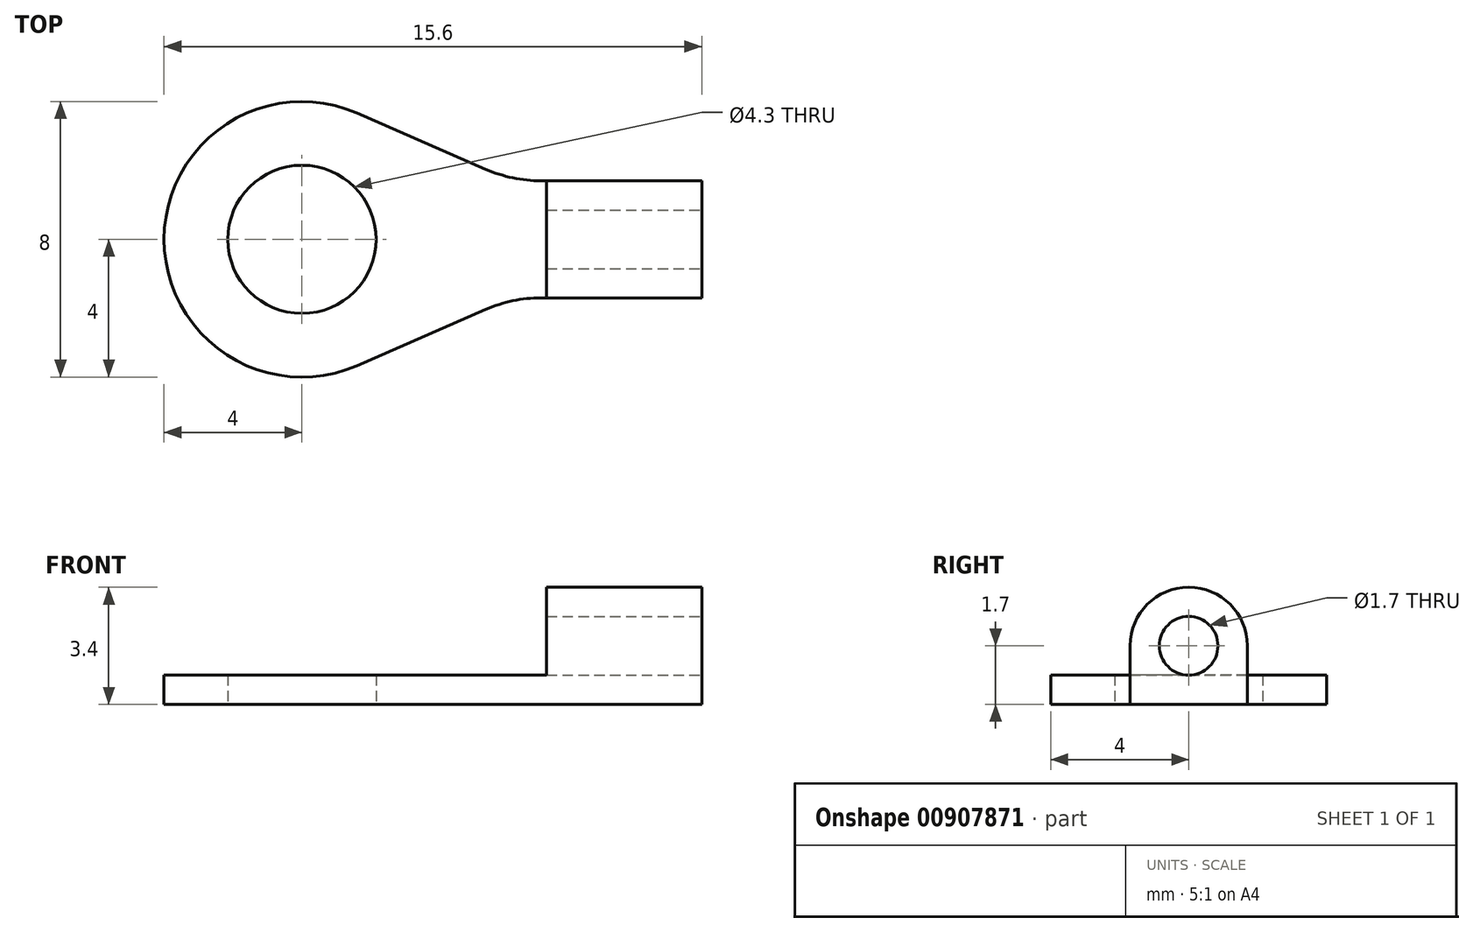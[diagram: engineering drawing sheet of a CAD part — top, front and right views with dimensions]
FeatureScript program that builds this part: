
annotation { "Feature Type Name" : "Feature", "Feature Type Description" : "" }
export const myFeature = defineFeature(function(context is Context, id is Id, definition is map)
    precondition{}
    {
        {
            var Q0;
            Q0=qCreatedBy(makeId("Top.planeOp"),FACE);
            var sketch = newSketch(context, id + "F0", { "sketchPlane" : qUnion([Q0])});
            skLineSegment(sketch, "E0.left", {"start": v(0, 4) * mm, "end": v(0, 4) * mm});
            skLineSegment(sketch, "E0.right", {"start": v(15.6, 2.3) * mm, "end": v(15.6, 5.7) * mm});
            skPoint(sketch, "E1.visualSharp", {"position": v(0, 8) * mm});
            skArc(sketch, "E1.filletArc", {"start": v(4, 8) * mm, "mid": v(1.17, 6.83) * mm, "end": v(0, 4) * mm});
            skPoint(sketch, "E2.visualSharp", {"position": v(0, 0) * mm});
            skArc(sketch, "E2.filletArc", {"start": v(0, 4) * mm, "mid": v(1.17, 1.17) * mm, "end": v(4, 0) * mm});
            skLineSegment(sketch, "E3.bottom", {"start": v(10.94, 2.3) * mm, "end": v(15.6, 2.3) * mm});
            skLineSegment(sketch, "E3.top", {"start": v(10.94, 5.7) * mm, "end": v(15.6, 5.7) * mm});
            skPoint(sketch, "E3.middle", {"position": v(15.6, 4) * mm});
            skArc(sketch, "E4", {"start": v(5.6, 7.67) * mm, "mid": v(0, 4) * mm, "end": v(5.6, 0.33) * mm});
            skCircle(sketch, "E5", {"center": v(4, 4) * mm, "radius": 2.15 * mm});
            skLineSegment(sketch, "E6", {"start": v(9.33, 6.03) * mm, "end": v(5.6, 7.67) * mm});
            skLineSegment(sketch, "E7", {"start": v(9.33, 1.97) * mm, "end": v(5.6, 0.33) * mm});
            skPoint(sketch, "E8.visualSharp", {"position": v(10.1, 5.7) * mm});
            skArc(sketch, "E8.filletArc", {"start": v(9.33, 6.03) * mm, "mid": v(10.12, 5.78) * mm, "end": v(10.94, 5.7) * mm});
            skPoint(sketch, "E9.visualSharp", {"position": v(10.1, 2.3) * mm});
            skArc(sketch, "E9.filletArc", {"start": v(10.94, 2.3) * mm, "mid": v(10.12, 2.22) * mm, "end": v(9.33, 1.97) * mm});
            skPoint(sketch, "E10.orphan", {"position": v(20.1, 5.7) * mm});
            skPoint(sketch, "E11.orphan", {"position": v(20.1, 2.3) * mm});
            skPoint(sketch, "E0.bottom.end.orphan", {"position": v(15.6, 0) * mm});
            skPoint(sketch, "E0.top.end.orphan", {"position": v(15.6, 8) * mm});
            skPoint(sketch, "E3.left.end.orphan", {"position": v(11.1, 5.7) * mm});
            skPoint(sketch, "E3.left.start.orphan", {"position": v(11.1, 2.3) * mm});
            skSolve(sketch);
        }
        {
            var Q0;
            Q0=makeQuery(id+"F0.imprint","IMPRINT",FACE,{"disambiguationData":[TD([[makeQuery(id+"F0.imprint","IMPRINT",EDGE,{"derivedFrom":sQuery(id+"F0.wireOp",EDGE,"E0.right")}),1.0]])]});
            extrude(context, id + "F1", {"entities" : qUnion([Q0]), "depth" : 0.85 * mm, "offsetDistance" : 25 * mm});
        }
        {
            var Q0;
            Q0=makeQuery(id+"F1.opExtrude","CAP_FACE",FACE,{"disambiguationData":[OSD([sQuery(id+"F0.wireOp",EDGE,"E0.right"),sQuery(id+"F0.wireOp",EDGE,"E3.bottom"),sQuery(id+"F0.wireOp",EDGE,"E3.top"),sQuery(id+"F0.wireOp",EDGE,"E4"),sQuery(id+"F0.wireOp",EDGE,"E5"),sQuery(id+"F0.wireOp",EDGE,"E6"),sQuery(id+"F0.wireOp",EDGE,"E7"),sQuery(id+"F0.wireOp",EDGE,"E8.filletArc"),sQuery(id+"F0.wireOp",EDGE,"E9.filletArc")])],"isStart":false});
            var sketch = newSketch(context, id + "F2", { "sketchPlane" : qUnion([Q0])});
            skLineSegment(sketch, "E12.bottom", {"start": v(15.6, 5.7) * mm, "end": v(11.1, 5.7) * mm});
            skLineSegment(sketch, "E12.top", {"start": v(15.6, 2.3) * mm, "end": v(11.1, 2.3) * mm});
            skLineSegment(sketch, "E12.left", {"start": v(15.6, 5.7) * mm, "end": v(15.6, 2.3) * mm});
            skLineSegment(sketch, "E12.right", {"start": v(11.1, 5.7) * mm, "end": v(11.1, 2.3) * mm});
            skSolve(sketch);
        }
        {
            var Q0;
            Q0=makeQuery(id+"F2.imprint","IMPRINT",FACE,{"disambiguationData":[TD([[makeQuery(id+"F2.imprint","IMPRINT",EDGE,{"derivedFrom":sQuery(id+"F2.wireOp",EDGE,"E12.bottom")}),-1.0]])]});
            extrude(context, id + "F3", {"entities" : qUnion([Q0]), "operationType" : NewBodyOperationType.ADD, "depth" : 2.55 * mm, "offsetDistance" : 25 * mm});
        }
        {
            var Q0;
            Q0=makeQuery(id+"F3.opExtrude","CAP_EDGE",EDGE,{"disambiguationData":[OSD([sQuery(id+"F2.wireOp",EDGE,"E12.bottom")])],"isStart":false});
            var Q1;
            Q1=makeQuery(id+"F3.opExtrude","CAP_EDGE",EDGE,{"disambiguationData":[OSD([sQuery(id+"F2.wireOp",EDGE,"E12.top")])],"isStart":false});
            fillet(context, id + "F4", {"entities" : qUnion([Q0, Q1]), "radius" : 1.7 * mm, "tangentPropagation" : true, "allowEdgeOverflow" : false});
        }
        {
            var Q0;
            Q0=makeQuery(id+"F3.boolean.opBoolean","MERGE",FACE,{"derivedFrom":[makeQuery(id+"F1.opExtrude","SWEPT_FACE",FACE,{"disambiguationData":[OSD([sQuery(id+"F0.wireOp",EDGE,"E0.right")])]}),makeQuery(id+"F3.opExtrude","SWEPT_FACE",FACE,{"disambiguationData":[OSD([sQuery(id+"F2.wireOp",EDGE,"E12.left")])]})]});
            var sketch = newSketch(context, id + "F5", { "sketchPlane" : qUnion([Q0])});
            skCircle(sketch, "E13", {"center": v(4, 1.7) * mm, "radius": 0.85 * mm});
            skSolve(sketch);
        }
        {
            var Q0;
            Q0=makeQuery(id+"F5.imprint","IMPRINT",FACE,{"disambiguationData":[TD([[makeQuery(id+"F5.imprint","IMPRINT",EDGE,{"derivedFrom":sQuery(id+"F5.wireOp",EDGE,"E13")}),1.0]])]});
            extrude(context, id + "F6", {"entities" : qUnion([Q0]), "operationType" : NewBodyOperationType.REMOVE, "oppositeDirection" : true, "depth" : 25 * mm, "offsetDistance" : 25 * mm});
        }
    });
